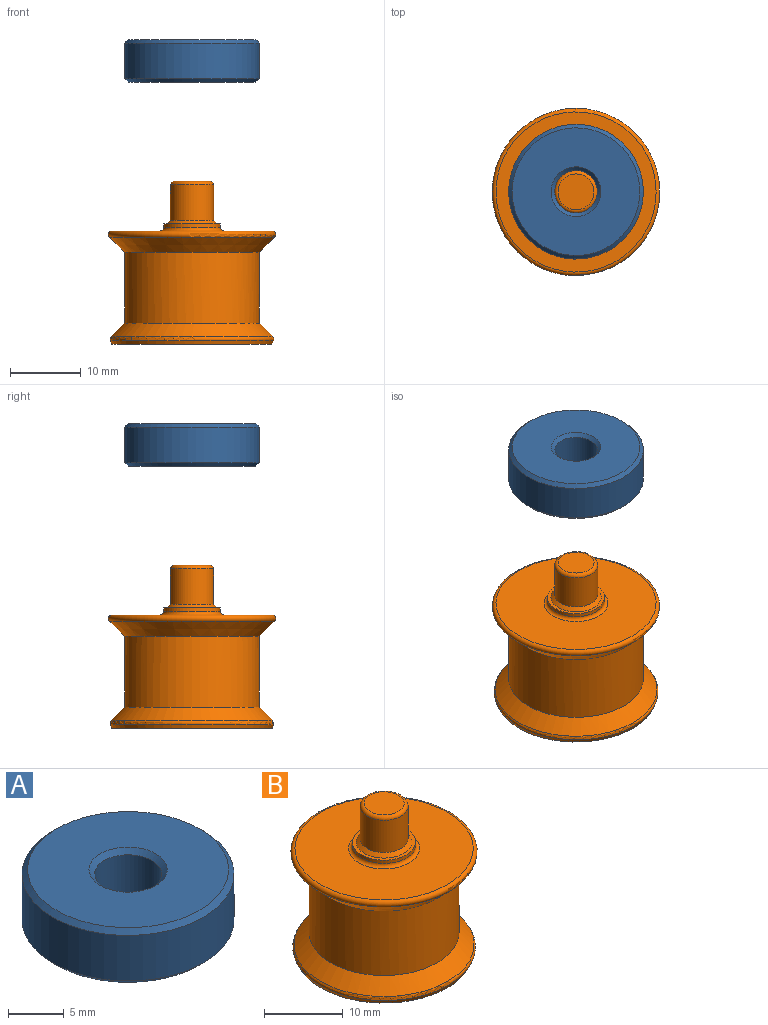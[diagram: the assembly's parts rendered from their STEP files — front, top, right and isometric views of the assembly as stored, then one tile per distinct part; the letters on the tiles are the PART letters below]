
ASSEMBLY  parts=2 mates=1
PART A: 8 faces, bbox 19x19x6 mm
  f0: cylinder r=3mm len=6mm, axis (0,0,-1), area 94.2mm2, adj f4,f6
  f1: cylinder r=9.5mm len=19mm, axis (0,0,-1), area 298.5mm2, adj f5,f7
  f2: plane 18x18mm, normal (0,0,1), area 216mm2, adj f6,f7
  f3: plane 18x18mm, normal (0,0,-1), area 216mm2, adj f4,f5
  f4: cone r=3.5mm half-angle=45deg, axis (0,0,-1), area 14.4mm2, adj f0,f3
  f5: cone r=9.5mm half-angle=45deg, axis (0,0,1), area 41.1mm2, adj f1,f3
  f6: cone r=3mm half-angle=45deg, axis (0,0,1), area 14.4mm2, adj f0,f2
  f7: cone r=9mm half-angle=45deg, axis (0,0,-1), area 41.1mm2, adj f1,f2
PART B: 19 faces, bbox 25.5x25.5x23 mm
  f0: cylinder r=4mm len=8mm, axis (0,0,-1), area 12.6mm2, adj f1,f16
  f1: plane 8x8mm, normal (0,0,1), area 11mm2, adj f0,f14
  f2: cylinder r=3.04mm len=6.08mm, axis (0,0,-1), area 95.4mm2, adj f14,f18
  f3: plane 5.08x5.08mm, normal (0,0,1), area 20.2mm2, adj f18
  f4: cone r=12.5mm half-angle=45deg, axis (0,0,1), area 201.7mm2, adj f6,f17
  f5: plane 22.59x22.59mm, normal (0,0,1), area 337mm2, adj f16,f17
  f6: cylinder r=9.5mm len=19mm, axis (0,0,1), area 596.9mm2, adj f4,f7
  f7: cone r=9.5mm half-angle=45deg, axis (0,0,-1), area 177.5mm2, adj f6,f15
  f8: plane 22.59x22.59mm, normal (0,0,-1), area 246.7mm2, adj f11,f13
  f9: cylinder r=6.5mm len=13mm, axis (0,0,-1), area 490.1mm2, adj f12,f13
  f10: plane 12x12mm, normal (0,0,-1), area 113.1mm2, adj f12
  f11: cone r=11.65mm half-angle=22.5deg, axis (0,0,1), area 42.3mm2, adj f8,f15
  f12: cone r=6mm half-angle=45deg, axis (0,0,-1), area 27.8mm2, adj f9,f10
  f13: cone r=6.5mm half-angle=45deg, axis (0,0,-1), area 30mm2, adj f8,f9
  f14: cone r=3.04mm half-angle=45deg, axis (0,0,-1), area 14.6mm2, adj f1,f2
  f15: torus R=11.06mm, axis (0,0,-1), area 42.6mm2, adj f7,f11
  f16: torus R=4.5mm, axis (0,0,1), area 20.6mm2, adj f0,f5
  f17: torus R=11.29mm, axis (0,0,1), area 86.3mm2, adj f4,f5
  f18: torus R=2.54mm, axis (0,0,1), area 14.1mm2, adj f2,f3
PLACE A t=(-8.16,2.63,43.01)mm
PLACE B t=(-8.16,2.63,22.01)mm
MATE fastened A.f0 <-> B.f2  axis (0,0,1) through (-8.16,2.63,49.01)mm
